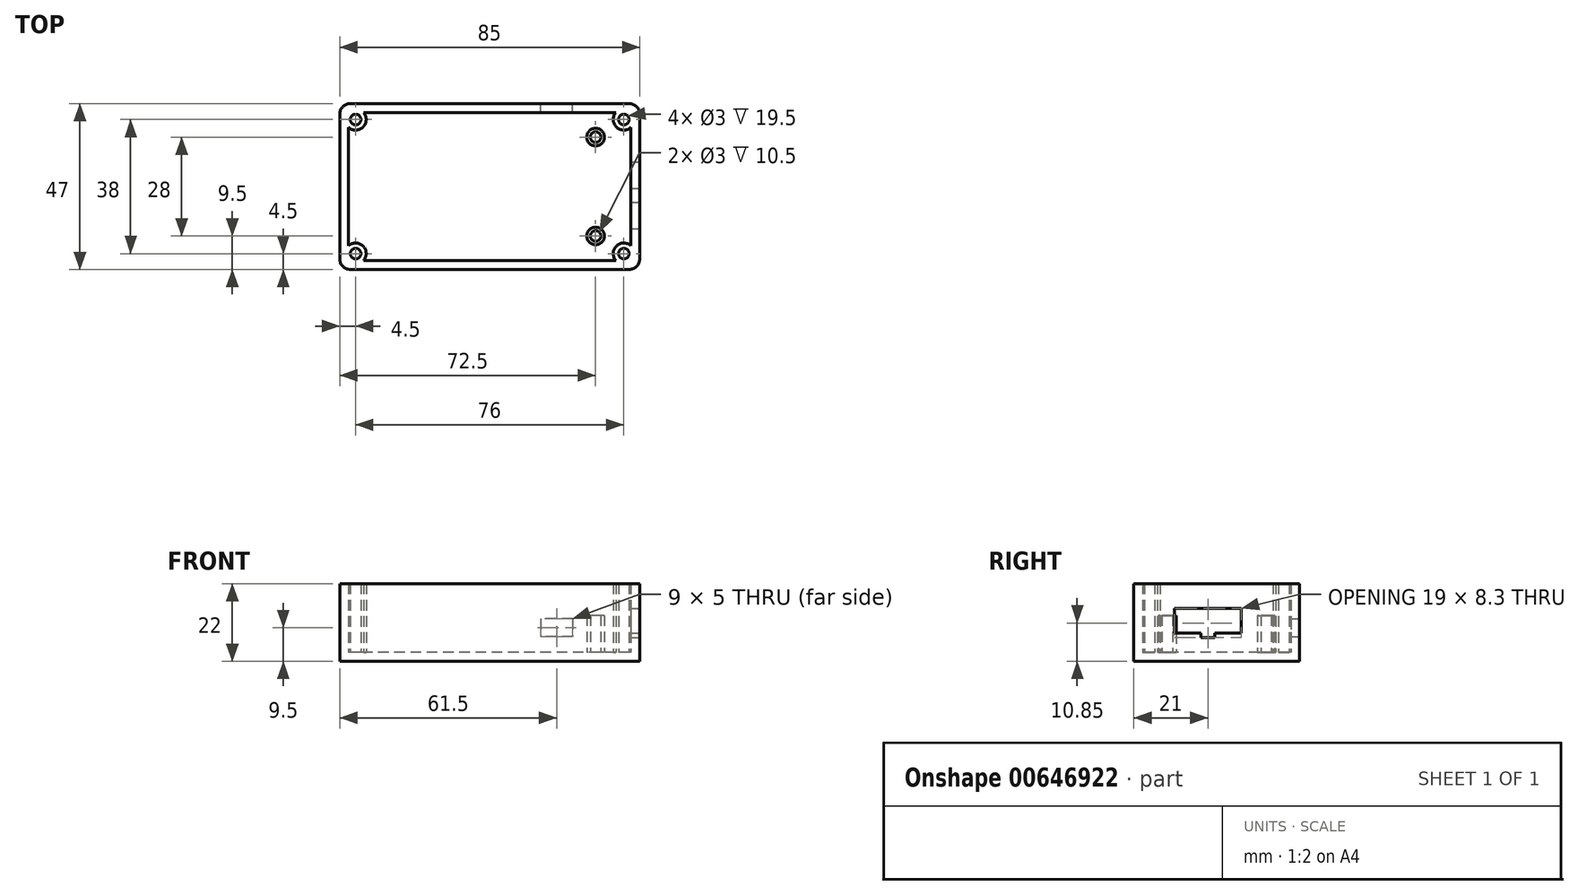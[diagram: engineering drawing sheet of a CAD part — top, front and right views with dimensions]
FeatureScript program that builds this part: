
annotation { "Feature Type Name" : "Feature", "Feature Type Description" : "" }
export const myFeature = defineFeature(function(context is Context, id is Id, definition is map)
    precondition{}
    {
        {
            var Q0;
            Q0=qCreatedBy(makeId("Top.planeOp"),FACE);
            var sketch = newSketch(context, id + "F0", { "sketchPlane" : qUnion([Q0])});
            skLineSegment(sketch, "E0.bottom", {"start": v(39.5, 23.5) * mm, "end": v(-39.5, 23.5) * mm});
            skLineSegment(sketch, "E0.top", {"start": v(39.5, -23.5) * mm, "end": v(-39.5, -23.5) * mm});
            skLineSegment(sketch, "E0.left", {"start": v(42.5, 20.5) * mm, "end": v(42.5, -20.5) * mm});
            skLineSegment(sketch, "E0.right", {"start": v(-42.5, 20.5) * mm, "end": v(-42.5, -20.5) * mm});
            skPoint(sketch, "E0.middle", {"position": v(0, 0) * mm});
            skPoint(sketch, "E1.visualSharp", {"position": v(-42.5, 23.5) * mm});
            skArc(sketch, "E1.filletArc", {"start": v(-39.5, 23.5) * mm, "mid": v(-41.62, 22.62) * mm, "end": v(-42.5, 20.5) * mm});
            skPoint(sketch, "E2.visualSharp", {"position": v(-42.5, -23.5) * mm});
            skArc(sketch, "E2.filletArc", {"start": v(-42.5, -20.5) * mm, "mid": v(-41.62, -22.62) * mm, "end": v(-39.5, -23.5) * mm});
            skPoint(sketch, "E3.visualSharp", {"position": v(42.5, 23.5) * mm});
            skArc(sketch, "E3.filletArc", {"start": v(42.5, 20.5) * mm, "mid": v(41.62, 22.62) * mm, "end": v(39.5, 23.5) * mm});
            skPoint(sketch, "E4.visualSharp", {"position": v(42.5, -23.5) * mm});
            skArc(sketch, "E4.filletArc", {"start": v(39.5, -23.5) * mm, "mid": v(41.62, -22.62) * mm, "end": v(42.5, -20.5) * mm});
            skSolve(sketch);
        }
        {
            var Q0;
            Q0 = qSketchRegion(id + "F0", true);
            extrude(context, id + "F1", {"entities" : qUnion([Q0]), "depth" : 22 * mm, "offsetDistance" : 25 * mm});
        }
        {
            var Q0;
            Q0=makeQuery(id+"F1.opExtrude","CAP_FACE",FACE,{"disambiguationData":[OSD([sQuery(id+"F0.wireOp",EDGE,"E0.bottom"),sQuery(id+"F0.wireOp",EDGE,"E0.top"),sQuery(id+"F0.wireOp",EDGE,"E0.left"),sQuery(id+"F0.wireOp",EDGE,"E0.right")])],"isStart":false});
            shell(context, id + "F2", {"entities" : qUnion([Q0]), "thickness" : 2.5 * mm});
        }
        {
            var Q0;
            Q0=makeQuery(id+"F2.opShell","OFFSET_FACE",FACE,{"disambiguationData":[OSD([sQuery(id+"F0.wireOp",EDGE,"E0.bottom"),sQuery(id+"F0.wireOp",EDGE,"E0.top"),sQuery(id+"F0.wireOp",EDGE,"E0.left"),sQuery(id+"F0.wireOp",EDGE,"E0.right")])]});
            var sketch = newSketch(context, id + "F3", { "sketchPlane" : qUnion([Q0])});
            skCircle(sketch, "E5", {"center": v(-38, 19) * mm, "radius": 3 * mm});
            skCircle(sketch, "E6.0", {"center": v(-38, 19) * mm, "radius": 1.5 * mm});
            skCircle(sketch, "E7.MirrorC", {"center": v(38, 19) * mm, "radius": 3 * mm});
            skCircle(sketch, "E8.MirrorC", {"center": v(38, 19) * mm, "radius": 1.5 * mm});
            skCircle(sketch, "E9.MirrorC", {"center": v(38, -19) * mm, "radius": 3 * mm});
            skCircle(sketch, "E10.MirrorC", {"center": v(38, -19) * mm, "radius": 1.5 * mm});
            skCircle(sketch, "E11.MirrorC", {"center": v(-38, -19) * mm, "radius": 3 * mm});
            skCircle(sketch, "E12.MirrorC", {"center": v(-38, -19) * mm, "radius": 1.5 * mm});
            skSolve(sketch);
        }
        {
            var Q0;
            Q0 = qSketchRegion(id + "F3", true);
            var Q1;
            Q1=makeQuery(id+"F1.opExtrude","CAP_FACE",FACE,{"disambiguationData":[OSD([sQuery(id+"F0.wireOp",EDGE,"E0.bottom"),sQuery(id+"F0.wireOp",EDGE,"E0.top"),sQuery(id+"F0.wireOp",EDGE,"E0.left"),sQuery(id+"F0.wireOp",EDGE,"E0.right")])],"isStart":false});
            extrude(context, id + "F4", {"entities" : qUnion([Q0]), "operationType" : NewBodyOperationType.ADD, "endBound" : BoundingType.UP_TO_SURFACE, "depth" : 25 * mm, "endBoundEntityFace" : qUnion([Q1]), "offsetDistance" : 25 * mm});
        }
        {
            var Q0;
            Q0=makeQuery(id+"F1.opExtrude","SWEPT_FACE",FACE,{"disambiguationData":[OSD([sQuery(id+"F0.wireOp",EDGE,"E0.left")])]});
            var sketch = newSketch(context, id + "F5", { "sketchPlane" : qUnion([Q0])});
            skLineSegment(sketch, "E13.top", {"start": v(-12, 15) * mm, "end": v(7, 15) * mm});
            skLineSegment(sketch, "E13.left", {"start": v(-12, 8) * mm, "end": v(-12, 15) * mm});
            skLineSegment(sketch, "E13.right", {"start": v(7, 8) * mm, "end": v(7, 15) * mm});
            skLineSegment(sketch, "E14", {"start": v(-12, 8) * mm, "end": v(-4.5, 8) * mm});
            skLineSegment(sketch, "E15", {"start": v(-4.5, 8) * mm, "end": v(-4.5, 6.7) * mm});
            skLineSegment(sketch, "E16", {"start": v(-4.5, 6.7) * mm, "end": v(-0.5, 6.7) * mm});
            skLineSegment(sketch, "E17", {"start": v(-0.5, 6.7) * mm, "end": v(-0.5, 8) * mm});
            skLineSegment(sketch, "E18", {"start": v(-0.5, 8) * mm, "end": v(7, 8) * mm});
            skSolve(sketch);
        }
        {
            var Q0;
            Q0 = qSketchRegion(id + "F5", true);
            var Q1;
            Q1=makeQuery(id+"F2.opShell","OFFSET_FACE",FACE,{"disambiguationData":[OSD([sQuery(id+"F0.wireOp",EDGE,"E0.left")])]});
            extrude(context, id + "F6", {"entities" : qUnion([Q0]), "operationType" : NewBodyOperationType.REMOVE, "endBound" : BoundingType.UP_TO_SURFACE, "oppositeDirection" : true, "depth" : 25 * mm, "endBoundEntityFace" : qUnion([Q1]), "offsetDistance" : 25 * mm});
        }
        {
            var Q0;
            Q0=makeQuery(id+"F1.opExtrude","SWEPT_FACE",FACE,{"disambiguationData":[OSD([sQuery(id+"F0.wireOp",EDGE,"E0.bottom")])]});
            var sketch = newSketch(context, id + "F7", { "sketchPlane" : qUnion([Q0])});
            skLineSegment(sketch, "E19.bottom", {"start": v(-23.5, 12) * mm, "end": v(-14.5, 12) * mm});
            skLineSegment(sketch, "E19.top", {"start": v(-23.5, 7) * mm, "end": v(-14.5, 7) * mm});
            skLineSegment(sketch, "E19.left", {"start": v(-23.5, 12) * mm, "end": v(-23.5, 7) * mm});
            skLineSegment(sketch, "E19.right", {"start": v(-14.5, 12) * mm, "end": v(-14.5, 7) * mm});
            skSolve(sketch);
        }
        {
            var Q0;
            Q0 = qSketchRegion(id + "F7", true);
            var Q1;
            Q1=makeQuery(id+"F2.opShell","OFFSET_FACE",FACE,{"disambiguationData":[OSD([sQuery(id+"F0.wireOp",EDGE,"E0.bottom")])]});
            extrude(context, id + "F8", {"entities" : qUnion([Q0]), "operationType" : NewBodyOperationType.REMOVE, "endBound" : BoundingType.UP_TO_SURFACE, "oppositeDirection" : true, "depth" : 25 * mm, "endBoundEntityFace" : qUnion([Q1]), "offsetDistance" : 25 * mm});
        }
        {
            var Q0;
            {var subQ0=sQuery(id+"F0.wireOp",EDGE,"E0.right");var subQ1=sQuery(id+"F0.wireOp",EDGE,"E0.left");var subQ2=sQuery(id+"F0.wireOp",EDGE,"E0.top");var subQ3=sQuery(id+"F0.wireOp",EDGE,"E0.bottom");Q0=makeQuery(id+"F4.boolean.opBoolean","SPLIT",FACE,{"disambiguationData":[TD([makeQuery(id+"F2.opShell","OFFSET_FACE",FACE,{"disambiguationData":[OSD([subQ3])]})])],"derivedFrom":makeQuery(id+"F2.opShell","OFFSET_FACE",FACE,{"disambiguationData":[OSD([subQ3,subQ2,subQ1,subQ0,sQuery(id+"F0.wireOp",EDGE,"E1.filletArc"),sQuery(id+"F0.wireOp",EDGE,"E2.filletArc"),sQuery(id+"F0.wireOp",EDGE,"E3.filletArc"),sQuery(id+"F0.wireOp",EDGE,"E4.filletArc")])]})});}
            var sketch = newSketch(context, id + "F9", { "sketchPlane" : qUnion([Q0])});
            skCircle(sketch, "E20", {"center": v(30, 14) * mm, "radius": 2.5 * mm});
            skCircle(sketch, "E21.0", {"center": v(30, 14) * mm, "radius": 1.5 * mm});
            skCircle(sketch, "E22.MirrorC", {"center": v(30, -14) * mm, "radius": 1.5 * mm});
            skCircle(sketch, "E23.MirrorC", {"center": v(30, -14) * mm, "radius": 2.5 * mm});
            skSolve(sketch);
        }
        {
            var Q0;
            Q0 = qSketchRegion(id + "F9", true);
            extrude(context, id + "F10", {"entities" : qUnion([Q0]), "operationType" : NewBodyOperationType.ADD, "depth" : 10.5 * mm, "offsetDistance" : 25 * mm});
        }
    });
